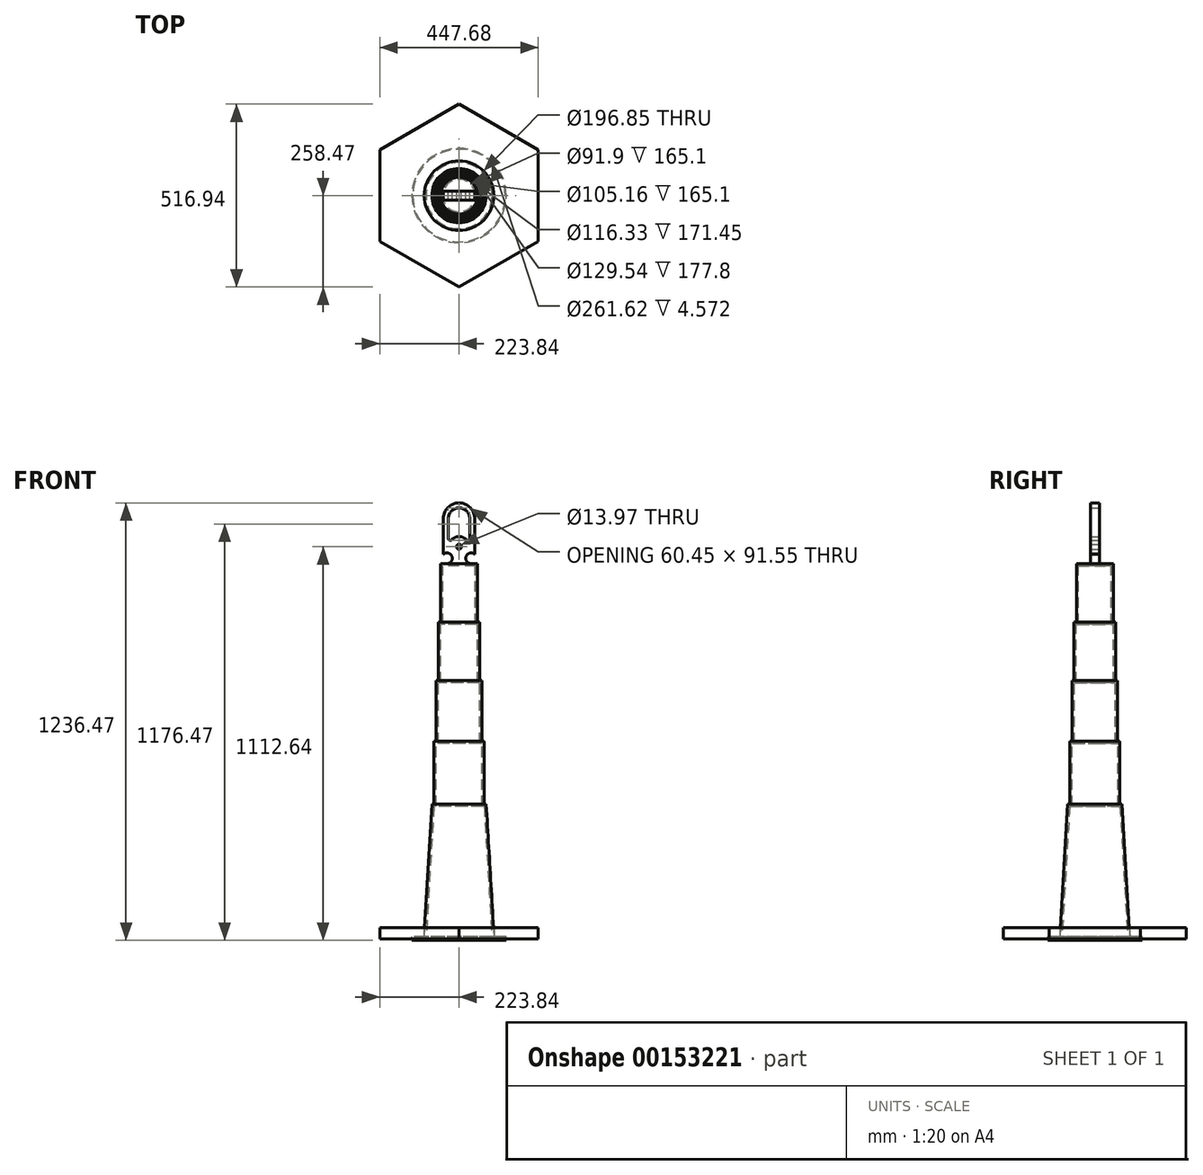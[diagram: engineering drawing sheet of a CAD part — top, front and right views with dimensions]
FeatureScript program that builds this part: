
annotation { "Feature Type Name" : "Feature", "Feature Type Description" : "" }
export const myFeature = defineFeature(function(context is Context, id is Id, definition is map)
    precondition{}
    {
        {
            var Q0;
            Q0=qCreatedBy(makeId("Front.planeOp"),FACE);
            var sketch = newSketch(context, id + "F0", { "sketchPlane" : qUnion([Q0])});
            skLineSegment(sketch, "E0", {"start": v(133.35, 6.1) * mm, "end": v(99.06, 6.1) * mm});
            skLineSegment(sketch, "E1", {"start": v(99.06, 6.1) * mm, "end": v(76.7, 381) * mm});
            skLineSegment(sketch, "E2", {"start": v(76.7, 381) * mm, "end": v(70.87, 381) * mm});
            skLineSegment(sketch, "E3", {"start": v(70.87, 381) * mm, "end": v(70.87, 558.8) * mm});
            skLineSegment(sketch, "E4", {"start": v(70.87, 558.8) * mm, "end": v(64.26, 558.8) * mm});
            skLineSegment(sketch, "E5", {"start": v(64.26, 558.8) * mm, "end": v(64.26, 730.25) * mm});
            skLineSegment(sketch, "E6", {"start": v(64.26, 730.25) * mm, "end": v(58.67, 730.25) * mm});
            skLineSegment(sketch, "E7", {"start": v(58.67, 730.25) * mm, "end": v(58.67, 895.35) * mm});
            skLineSegment(sketch, "E8", {"start": v(58.67, 895.35) * mm, "end": v(52.04, 895.35) * mm});
            skLineSegment(sketch, "E9", {"start": v(52.04, 895.35) * mm, "end": v(52.04, 1060.45) * mm});
            skLineSegment(sketch, "E10", {"start": v(52.04, 1060.45) * mm, "end": v(0, 1060.45) * mm});
            skLineSegment(sketch, "E11", {"start": v(0, 1060.45) * mm, "end": v(0, 1054.35) * mm});
            skLineSegment(sketch, "E12", {"start": v(0, 1054.35) * mm, "end": v(45.95, 1054.35) * mm});
            skLineSegment(sketch, "E13", {"start": v(45.95, 1054.35) * mm, "end": v(45.95, 889.25) * mm});
            skLineSegment(sketch, "E14", {"start": v(45.95, 889.25) * mm, "end": v(52.58, 889.25) * mm});
            skLineSegment(sketch, "E15", {"start": v(52.58, 889.25) * mm, "end": v(52.58, 724.15) * mm});
            skLineSegment(sketch, "E16", {"start": v(52.58, 724.15) * mm, "end": v(58.17, 724.15) * mm});
            skLineSegment(sketch, "E17", {"start": v(58.17, 724.15) * mm, "end": v(58.17, 552.7) * mm});
            skLineSegment(sketch, "E18", {"start": v(58.17, 552.7) * mm, "end": v(64.77, 552.7) * mm});
            skLineSegment(sketch, "E19", {"start": v(64.77, 552.7) * mm, "end": v(64.77, 374.9) * mm});
            skLineSegment(sketch, "E20", {"start": v(64.77, 374.9) * mm, "end": v(70.96, 374.9) * mm});
            skLineSegment(sketch, "E21", {"start": v(70.96, 374.9) * mm, "end": v(93.32, 0) * mm});
            skLineSegment(sketch, "E22", {"start": v(133.35, 6.1) * mm, "end": v(133.35, -4.57) * mm});
            skLineSegment(sketch, "E23", {"start": v(133.35, -4.57) * mm, "end": v(130.81, -4.57) * mm});
            skLineSegment(sketch, "E24", {"start": v(130.81, -4.57) * mm, "end": v(130.81, 0) * mm});
            skLineSegment(sketch, "E25", {"start": v(130.81, 0) * mm, "end": v(93.32, 0) * mm});
            skArc(sketch, "E26", {"start": v(44.45, 1187.45) * mm, "mid": v(0, 1231.9) * mm, "end": v(-44.45, 1187.45) * mm});
            skLineSegment(sketch, "E27", {"start": v(0, 1231.9) * mm, "end": v(12.7, 1231.9) * mm, "construction": true});
            skLineSegment(sketch, "E28", {"start": v(44.45, 1187.45) * mm, "end": v(44.45, 1060.45) * mm});
            skPoint(sketch, "E28.endSnap0", {"position": v(26.02, 1060.45) * mm});
            skLineSegment(sketch, "E29", {"start": v(-44.45, 1187.45) * mm, "end": v(-44.45, 1060.45) * mm});
            skLineSegment(sketch, "E30", {"start": v(-44.45, 1060.45) * mm, "end": v(0, 1060.45) * mm});
            skArc(sketch, "E31", {"start": v(-34.13, 1060.45) * mm, "mid": v(-20.1, 1081.08) * mm, "end": v(-44.45, 1086.53) * mm});
            skLineSegment(sketch, "E32", {"start": v(-19.05, 1075.53) * mm, "end": v(-19.05, 1088.23) * mm, "construction": true});
            skArc(sketch, "E33.MirrorCS", {"start": v(34.13, 1060.45) * mm, "mid": v(20.1, 1081.08) * mm, "end": v(44.45, 1086.53) * mm});
            skArc(sketch, "E34", {"start": v(30.23, 1187.45) * mm, "mid": v(0, 1217.68) * mm, "end": v(-30.23, 1187.45) * mm});
            skPoint(sketch, "E35", {"position": v(0, 1108.08) * mm});
            skCircle(sketch, "E36", {"center": v(0, 1108.08) * mm, "radius": 6.99 * mm});
            skArc(sketch, "E37", {"start": v(20.65, 1127.82) * mm, "mid": v(0, 1136.65) * mm, "end": v(-20.65, 1127.82) * mm});
            skLineSegment(sketch, "E38", {"start": v(-30.23, 1187.45) * mm, "end": v(-30.23, 1131.66) * mm});
            skLineSegment(sketch, "E39", {"start": v(30.23, 1187.45) * mm, "end": v(30.23, 1131.66) * mm});
            skCircle(sketch, "E40", {"center": v(-24.67, 1131.66) * mm, "radius": 5.56 * mm, "construction": true});
            skArc(sketch, "E41", {"start": v(-30.23, 1131.66) * mm, "mid": v(-26.74, 1126.5) * mm, "end": v(-20.65, 1127.82) * mm});
            skArc(sketch, "E42.MirrorCS", {"start": v(30.23, 1131.66) * mm, "mid": v(26.74, 1126.5) * mm, "end": v(20.65, 1127.82) * mm});
            skSolve(sketch);
        }
        {
            var Q0;
            Q0=makeQuery(id+"F0.imprint","IMPRINT",FACE,{"disambiguationData":[TD([[makeQuery(id+"F0.imprint","IMPRINT",EDGE,{"derivedFrom":sQuery(id+"F0.wireOp",EDGE,"E0")}),1.0]])]});
            var Q1;
            Q1=sQuery(id+"F0.wireOp",EDGE,"E11");
            revolve(context, id + "F1", {"entities" : qUnion([Q0]), "axis" : qUnion([Q1]), "revolveType" : RevolveType.FULL});
        }
        {
            var Q0;
            {var subQ1=sQuery(id+"F0.wireOp",EDGE,"E26");Q0=makeQuery(id+"F0.imprint","IMPRINT",FACE,{"disambiguationData":[TD([[makeQuery(id+"F0.imprint","IMPRINT",EDGE,{"derivedFrom":subQ1}),1.0]])]});}
            extrude(context, id + "F2", {"entities" : qUnion([Q0]), "operationType" : NewBodyOperationType.ADD, "depth" : 12.7 * mm, "hasSecondDirection" : true, "secondDirectionOppositeDirection" : true, "secondDirectionDepth" : 12.7 * mm});
        }
        {
            var Q0;
            Q0=qCreatedBy(makeId("Top.planeOp"),FACE);
            var sketch = newSketch(context, id + "F3", { "sketchPlane" : qUnion([Q0])});
            skCircle(sketch, "E43.cCircle", {"center": v(0, 0) * mm, "radius": 223.84 * mm, "construction": true});
            skLineSegment(sketch, "E43.0", {"start": v(223.84, 129.23) * mm, "end": v(223.84, -129.23) * mm});
            skLineSegment(sketch, "E43.1", {"start": v(223.84, -129.23) * mm, "end": v(0, -258.47) * mm});
            skLineSegment(sketch, "E43.2", {"start": v(0, -258.47) * mm, "end": v(-223.84, -129.23) * mm});
            skLineSegment(sketch, "E43.3", {"start": v(-223.84, -129.23) * mm, "end": v(-223.84, 129.23) * mm});
            skLineSegment(sketch, "E43.4", {"start": v(-223.84, 129.23) * mm, "end": v(0, 258.47) * mm});
            skLineSegment(sketch, "E43.5", {"start": v(0, 258.47) * mm, "end": v(223.84, 129.23) * mm});
            skPoint(sketch, "E43.0.midPoint", {"position": v(223.84, 0) * mm});
            skCircle(sketch, "E44", {"center": v(0, 0) * mm, "radius": 98.43 * mm});
            skSolve(sketch);
        }
        {
            var Q0;
            Q0=makeQuery(id+"F3.imprint","IMPRINT",FACE,{"disambiguationData":[TD([[makeQuery(id+"F3.imprint","IMPRINT",EDGE,{"derivedFrom":sQuery(id+"F3.wireOp",EDGE,"E43.0")}),-1.0]])]});
            extrude(context, id + "F4", {"entities" : qUnion([Q0]), "depth" : 31.75 * mm});
        }
    });
